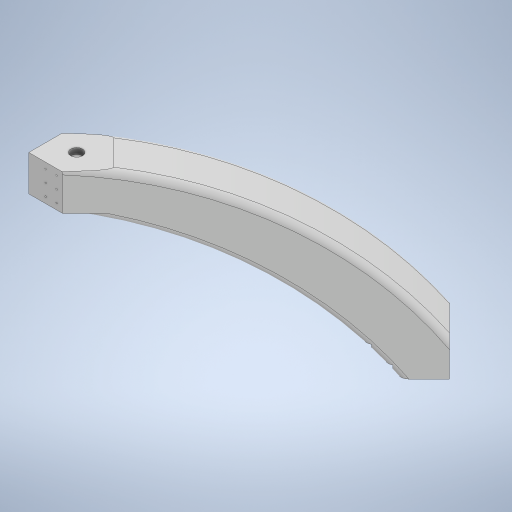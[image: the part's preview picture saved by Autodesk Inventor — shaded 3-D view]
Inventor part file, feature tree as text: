
AUTODESK INVENTOR PART (.ipt)
format: ipt  version: 2023 (Build 270158000, 158)  size: 475,136 bytes
history: native  units: in
note: dims shown in document units (in); Inventor stores cm internally (conversion verified against a paired STEP export)
features: other x16, sketch x9, extrude x8, hole x2, fillet x1
ambient origin geometry x8: Origin, YZ Plane, XZ Plane, XY Plane, X Axis, Y Axis, Z Axis, Center Point
bodies: Solid1 (feature_tree)
feature tree (36):
  sketch  "Sketch1"  dims[d0=54.0in d1=54.0in]
  sketch  "Sketch2"  dims[d2=1.0in d3=1.0in]
  extrude  "Extrusion1"  Depth=54.0in
  other  "Work Axis1"
  other  "Work Axis2"
  extrude  "Extrusion2"  Depth=1.0in
  sketch  "Sketch4"  dims[d36=0.25in d37=0.25in]
  extrude  "Extrusion3"  Depth=0.25in
  extrude  "Extrusion4"  Depth=0.25in
  extrude  "Extrusion5"  Depth=0.25in
  fillet  "Fillet1"  Radius=0.25in
  other  "Work Axis3"
  other  "Work Axis4"
  other  "Work Axis5"
  other  "Work Axis6"
  other  "Work Axis7"
  other  "Work Axis8"
  other  "Work Point2"
  other  "Work Point3"
  other  "Work Point4"
  other  "Work Point5"
  other  "Work Axis9"
  extrude  "Extrusion6"  Depth=2.0in
  extrude  "Extrusion7"  Depth=2.0in
  extrude  "Extrusion8"  Depth=12.0in
  other  "Work Point6"
  hole  "Hole1"  [1 undecoded]
  hole  "Hole2"  [1 undecoded]
  other  "Work Point1"
  sketch  "Sketch3"  dims[d34=0.25in d35=0.25in]
  sketch  "Sketch5"  dims[d38=0.25in d39=0.25in d40=0.25in]
  sketch  "Sketch6"  dims[d41=0.25in d42=2.0in]
  sketch  "Sketch7"  dims[d43=2.0in d44=2.0in]
  sketch  "Sketch8"  dims[d45=2.0in d46=12.0in]
  sketch  "Sketch9"  dims[d47=12.0in d48=12.0in d50=12.0in d51=15.0in d52=15.0in d53=15.0in d54=15.0in d55=15.0in d56=0.0in d57=3.0in d58=3.0in d59=3.0in d60=3.0in d61=30.0in d62=30.0in d63=15.0in d64=0.0in d65=0.125in d66=0.125in d67=0.125in d68=0.125in d69=0.125in d70=0.5in d71=1.414in d72=0.5in d73=0.5in d74=0.5in d75=0.5in d76=0.5in d77=1.414in d78=1.5in d79=1.414in d80=0.125in d81=0.125in d83=0.125in d84=0.125in d85=0.5in d86=0.5in d87=0.5in d88=1.414in d91=0.5in d92=0.5in d93=0.5in d94=1.414in d95=0.125in d96=1.5in d97=0.5in d98=0.125in d99=0.125in d100=1.414in d101=1.5in d102=1.5in d103=0.5in d104=1.0in d105=0.0in d106=1.0in d107=0.0in d108=0.25in d109=0.25in d110=0.25in d111=0.25in d112=0.25in d113=0.25in d114=0.75in d115=0.75in d116=2.0in d117=0.75in d118=0.75in d119=0.75in d120=0.75in d121=0.75in d122=2.0in d123=0.75in d124=0.75in d125=0.75in d126=10.0in d127=0.0in d128=0.5in d129=0.25in d130=0.25in d131=10.0in d132=0.0in d133=0.25in d134=2.0in d135=2.0in d136=1.0in d137=0.49in d138=0.0in d139=0.25in d140=3.0in d141=0.0in d142=1.0in d143=1.0in d144=1.0in d145=0.75in d146=0.375in d147=0.25in d148=0.5635in d149=1.0in d150=0.0in d151=1.0in d152=1.0in d153=1.0in d154=0.75in d155=0.375in d156=0.25in d157=0.5635in d158=1.0in d159=0.0in]
  other  "Work Axis10"
note: 2 required parameter values undecoded (feature->parameter linkage not recoverable at this tier; creation-order binding heuristic only, values carry confidence <= 0.55)
